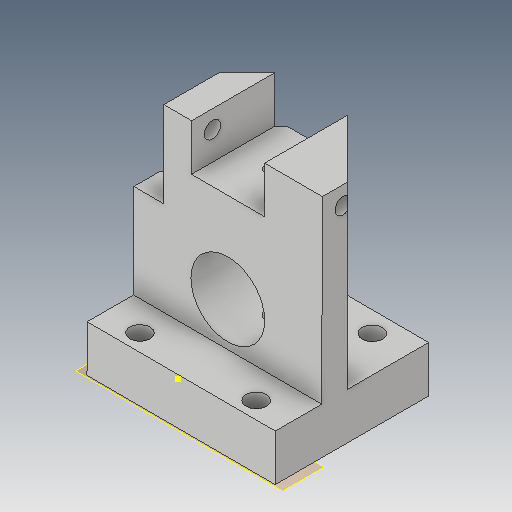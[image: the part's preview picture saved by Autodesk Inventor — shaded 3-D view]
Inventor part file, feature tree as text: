
AUTODESK INVENTOR PART (.ipt)
format: ipt  version: 2019.4 (Build 234330000, 330)  size: 220,160 bytes
history: native  units: mm
features: reference x11, sketch x7, other x7, extrude x6, plane x3, projected_geometry x2
ambient origin geometry x8: Origin, YZ Plane, XZ Plane, XY Plane, X Axis, Y Axis, Z Axis, Center Point
bodies: Body1 (feature_tree)
feature tree (36):
  plane  "Work Plane5"
  extrude  "Extrusion4"  TaperAngle=45.0deg  [1 undecoded]
  sketch  "Sketch7"  dims[d26=45.0deg d27=3.0mm]
  sketch  "Sketch8"  dims[d28=11.0mm d29=11.0mm]
  plane  "Work Plane7"
  extrude  "Extrusion5"  Depth=3.0mm
  sketch  "Sketch9"  dims[d30=8.0mm d31=10.0mm d32=0.0mm]
  plane  "Work Plane8"
  extrude  "Extrusion6"  Depth=11.0mm
  extrude  "Extrusion7"  Depth=10.0mm TaperAngle=0.0deg
  extrude  "Extrusion8"  Depth=0.3mm
  extrude  "Extrusion9"  Depth=10.0mm
  sketch  "Sketch5"  dims[d18=8.0mm d19=0.0mm d25=45.0deg]
  reference  "Reference18"
  reference  "Reference19"
  reference  "Reference20"
  reference  "Reference21"
  projected_geometry  "Projected Loop3"
  reference  "Reference23"
  reference  "Reference24"
  reference  "Reference25"
  reference  "Reference26"
  sketch  "Sketch10"  dims[d34=0.3mm d35=0.3mm]
  projected_geometry  "Projected Loop4"
  sketch  "Sketch11"  dims[d36=10.0mm d37=0.0mm d38=2.8mm]
  reference  "Reference27"
  sketch  "Sketch12"  dims[d39=10.0mm d40=0.0mm d41=0.7mm d42=10.0mm d43=0.0mm d44=0.0mm d45=0.0mm d46=2.8mm]
  reference  "Reference28"
  reference  "Reference29"
  other  "Assembly_opentrons_microscope_slide_y.iam"
  other  "00_MGN12H, LINEAR GUIDE BLOCK:2"
  other  "00_MGN12 LINEAR GUIDE RAIL, CONFIGURABLE:1"
  other  "Assembly_Opentrons_Imagingunit_v3.iam"
  other  "Assembly_Opentrons_Autofocus_v2:1"
  other  "01_Slide_camera_v1:1"
  other  "06_Fluorescence_Arm:1"
note: 1 required parameter value undecoded (feature->parameter linkage not recoverable at this tier; creation-order binding heuristic only, values carry confidence <= 0.55)
